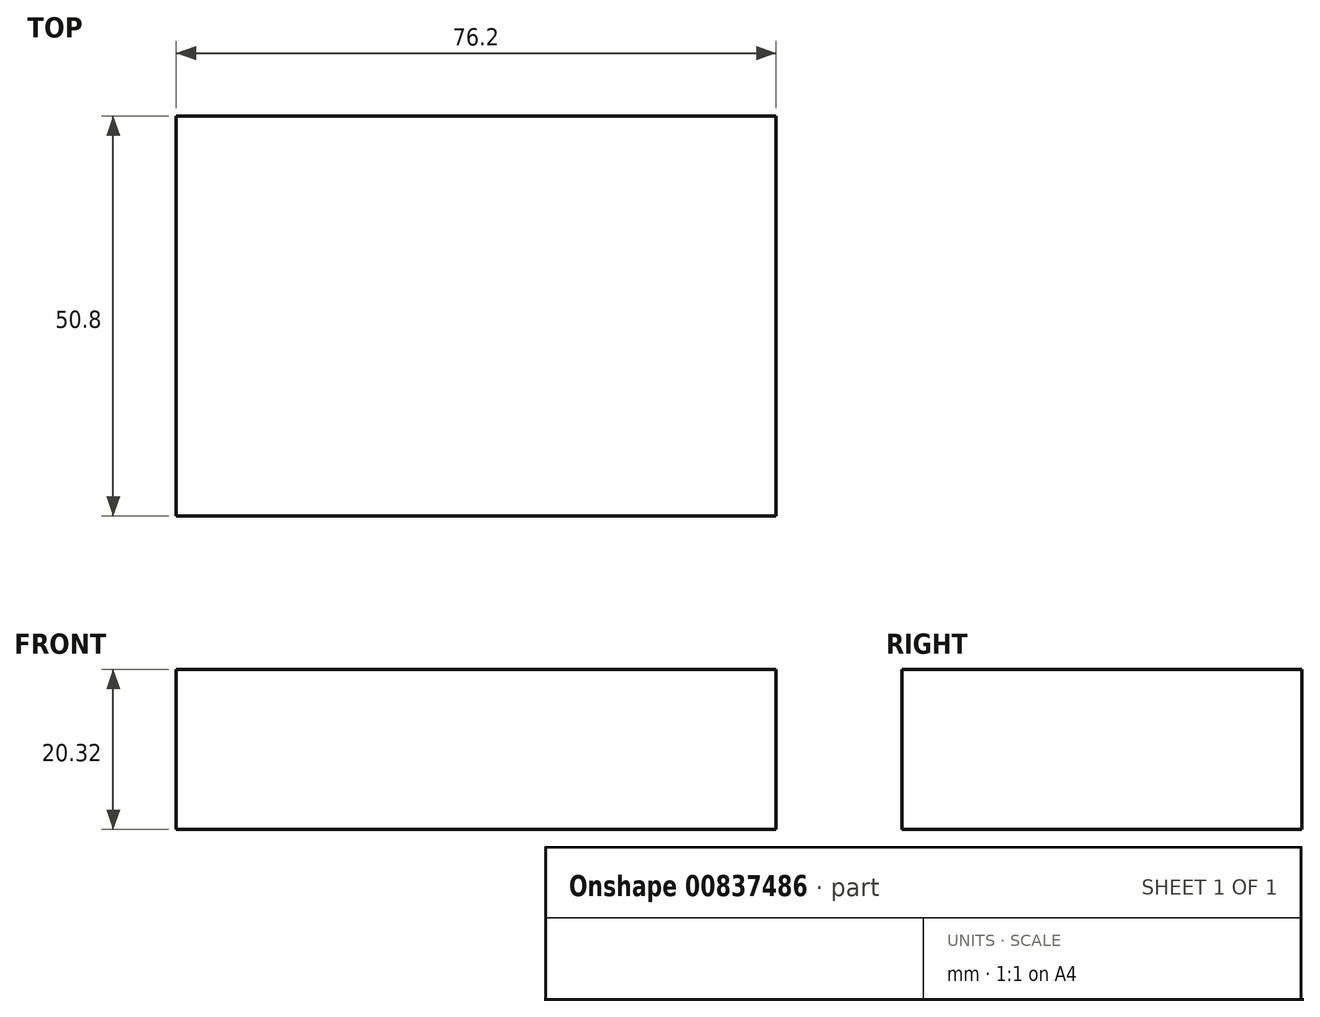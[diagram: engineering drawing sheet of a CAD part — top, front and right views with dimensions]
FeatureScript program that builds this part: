
annotation { "Feature Type Name" : "Feature", "Feature Type Description" : "" }
export const myFeature = defineFeature(function(context is Context, id is Id, definition is map)
    precondition{}
    {
        {
            var Q0;
            Q0=qCreatedBy(makeId("Front.planeOp"),FACE);
            var sketch = newSketch(context, id + "F0", { "sketchPlane" : qUnion([Q0])});
            skLineSegment(sketch, "E0", {"start": v(0, 0) * mm, "end": v(-38.1, 0) * mm});
            skLineSegment(sketch, "E1.MirrorCS", {"start": v(0, 0) * mm, "end": v(38.1, 0) * mm});
            skLineSegment(sketch, "E2", {"start": v(-38.1, 0) * mm, "end": v(-38.1, 20.32) * mm});
            skLineSegment(sketch, "E3", {"start": v(-38.1, 20.32) * mm, "end": v(38.1, 20.32) * mm});
            skLineSegment(sketch, "E4", {"start": v(38.1, 20.32) * mm, "end": v(38.1, 0) * mm});
            skSolve(sketch);
        }
        {
            var Q0;
            Q0=makeQuery(id+"F0.imprint","IMPRINT",FACE,{"disambiguationData":[TD([[makeQuery(id+"F0.imprint","IMPRINT",EDGE,{"derivedFrom":sQuery(id+"F0.wireOp",EDGE,"E0")}),-1.0]])]});
            extrude(context, id + "F1", {"entities" : qUnion([Q0]), "oppositeDirection" : true, "depth" : 50.8 * mm, "offsetDistance" : 25.4 * mm});
        }
    });
